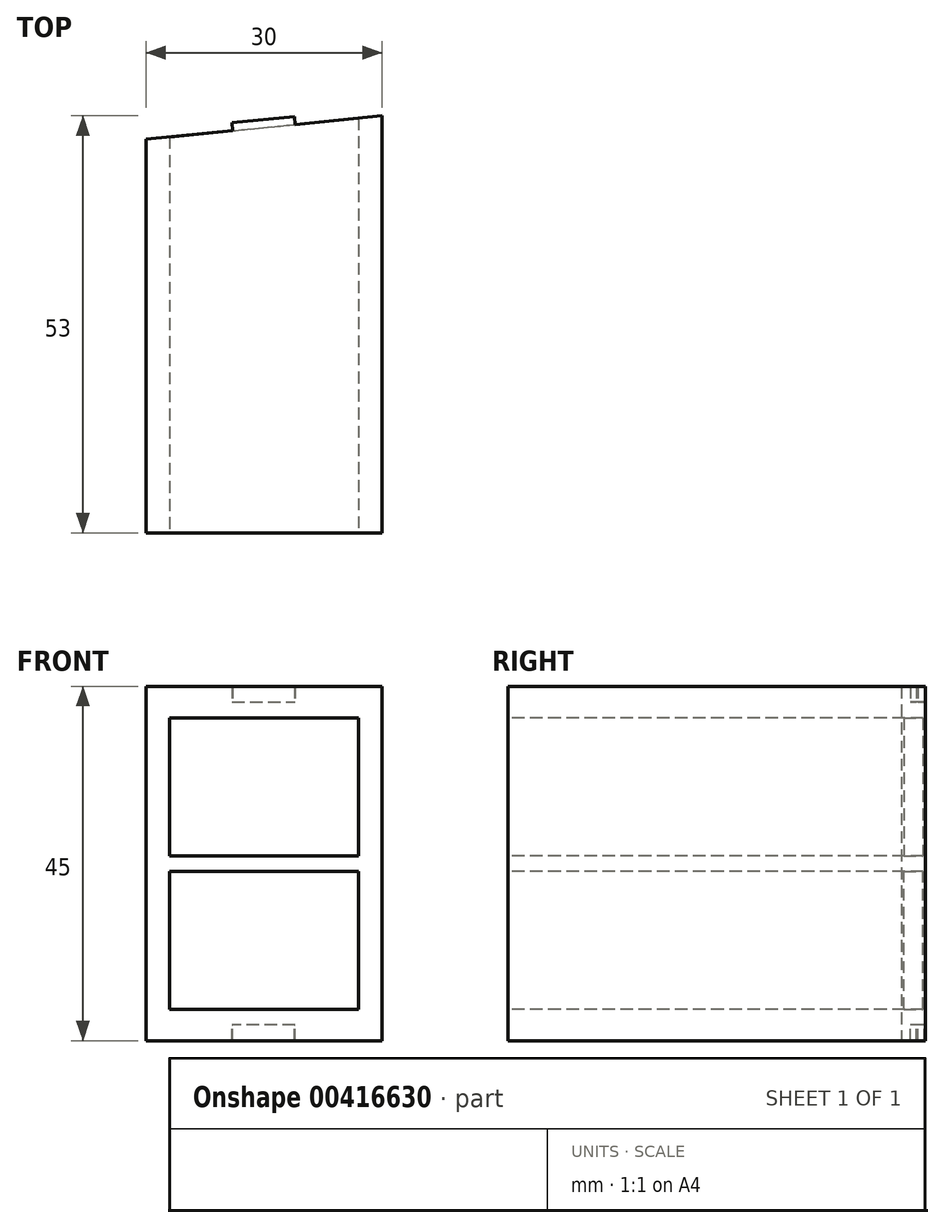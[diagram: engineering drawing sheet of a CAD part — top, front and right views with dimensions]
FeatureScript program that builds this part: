
annotation { "Feature Type Name" : "Feature", "Feature Type Description" : "" }
export const myFeature = defineFeature(function(context is Context, id is Id, definition is map)
    precondition{}
    {
        {
            assignVariable(context, id + "F0", {"name" : "E", "anyValue" : 45});
        }
        {
            var Q0;
            Q0=qCreatedBy(makeId("Top.planeOp"),FACE);
            var sketch = newSketch(context, id + "F1", { "sketchPlane" : qUnion([Q0])});
            skLineSegment(sketch, "E0", {"start": v(0, 0) * mm, "end": v(30, 0) * mm});
            skLineSegment(sketch, "E1", {"start": v(30, 0) * mm, "end": v(30, 3) * mm});
            skLineSegment(sketch, "E2", {"start": v(30, 3) * mm, "end": v(0, 0) * mm});
            skLineSegment(sketch, "E3", {"start": v(0, 0) * mm, "end": v(0, -50) * mm});
            skLineSegment(sketch, "E4", {"start": v(0, -50) * mm, "end": v(30, -50) * mm});
            skLineSegment(sketch, "E5", {"start": v(30, -50) * mm, "end": v(30, 0) * mm});
            skSolve(sketch);
        }
        {
            var Q0;
            Q0 = qSketchRegion(id + "F1", true);
            extrude(context, id + "F2", {"entities" : qUnion([Q0]), "depth" : (getVariable(context, 'E')) * mm});
        }
        {
            var Q0;
            Q0=makeQuery(id+"F2.opExtrude","SWEPT_FACE",FACE,{"disambiguationData":[OSD([sQuery(id+"F1.wireOp",EDGE,"E2")])]});
            var sketch = newSketch(context, id + "F3", { "sketchPlane" : qUnion([Q0])});
            skLineSegment(sketch, "E6", {"start": v(-30.15, 22.5) * mm, "end": v(0, 22.5) * mm, "construction": true});
            skLineSegment(sketch, "E7.bottom", {"start": v(-15.07, 0) * mm, "end": v(-11.07, 0) * mm});
            skLineSegment(sketch, "E7.top", {"start": v(-15.07, 2) * mm, "end": v(-11.07, 2) * mm});
            skLineSegment(sketch, "E7.left", {"start": v(-15.07, 0) * mm, "end": v(-15.07, 2) * mm});
            skLineSegment(sketch, "E7.right", {"start": v(-11.07, 0) * mm, "end": v(-11.07, 2) * mm});
            skLineSegment(sketch, "E8", {"start": v(-15.07, 45) * mm, "end": v(-15.07, 0) * mm, "construction": true});
            skLineSegment(sketch, "E9.MirrorCS", {"start": v(-15.07, 45) * mm, "end": v(-11.07, 45) * mm});
            skLineSegment(sketch, "E10.MirrorCS", {"start": v(-11.07, 45) * mm, "end": v(-11.07, 43) * mm});
            skLineSegment(sketch, "E11.MirrorCS", {"start": v(-15.07, 43) * mm, "end": v(-11.07, 43) * mm});
            skLineSegment(sketch, "E12.MirrorCS", {"start": v(-15.07, 0) * mm, "end": v(-19.07, 0) * mm});
            skLineSegment(sketch, "E13.MirrorCS", {"start": v(-15.07, 2) * mm, "end": v(-19.07, 2) * mm});
            skLineSegment(sketch, "E14.MirrorCS", {"start": v(-19.07, 0) * mm, "end": v(-19.07, 2) * mm});
            skLineSegment(sketch, "E15.MirrorCS", {"start": v(-15.07, 43) * mm, "end": v(-19.07, 43) * mm});
            skLineSegment(sketch, "E16.MirrorCS", {"start": v(-19.07, 45) * mm, "end": v(-19.07, 43) * mm});
            skLineSegment(sketch, "E17.MirrorCS", {"start": v(-15.07, 45) * mm, "end": v(-19.07, 45) * mm});
            skSolve(sketch);
        }
        {
            var Q0;
            Q0 = qSketchRegion(id + "F3", true);
            extrude(context, id + "F4", {"entities" : qUnion([Q0]), "operationType" : NewBodyOperationType.ADD, "depth" : 1 * mm});
        }
        {
            var Q0;
            Q0=makeQuery(id+"F2.opExtrude","SWEPT_FACE",FACE,{"disambiguationData":[OSD([sQuery(id+"F1.wireOp",EDGE,"E4")])]});
            var sketch = newSketch(context, id + "F5", { "sketchPlane" : qUnion([Q0])});
            skLineSegment(sketch, "E18", {"start": v(0, 22.5) * mm, "end": v(30, 22.5) * mm, "construction": true});
            skLineSegment(sketch, "E19.bottom", {"start": v(3, 4) * mm, "end": v(27, 4) * mm});
            skLineSegment(sketch, "E19.top", {"start": v(3, 21.5) * mm, "end": v(27, 21.5) * mm});
            skLineSegment(sketch, "E19.left", {"start": v(3, 4) * mm, "end": v(3, 21.5) * mm});
            skLineSegment(sketch, "E19.right", {"start": v(27, 4) * mm, "end": v(27, 21.5) * mm});
            skLineSegment(sketch, "E20.MirrorCS", {"start": v(3, 41) * mm, "end": v(3, 23.5) * mm});
            skLineSegment(sketch, "E21.MirrorCS", {"start": v(3, 41) * mm, "end": v(27, 41) * mm});
            skLineSegment(sketch, "E22.MirrorCS", {"start": v(3, 23.5) * mm, "end": v(27, 23.5) * mm});
            skLineSegment(sketch, "E23.MirrorCS", {"start": v(27, 41) * mm, "end": v(27, 23.5) * mm});
            skSolve(sketch);
        }
        {
            var Q0;
            Q0 = qSketchRegion(id + "F5", true);
            extrude(context, id + "F6", {"entities" : qUnion([Q0]), "operationType" : NewBodyOperationType.REMOVE, "endBound" : BoundingType.THROUGH_ALL, "oppositeDirection" : true, "depth" : 25 * mm});
        }
    });
